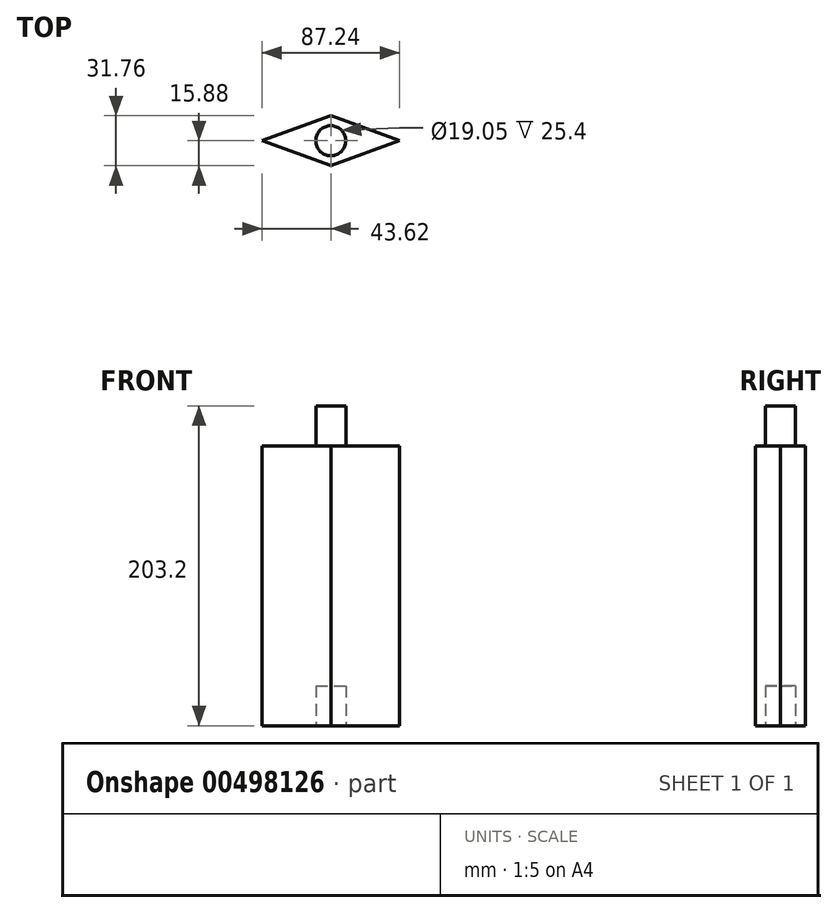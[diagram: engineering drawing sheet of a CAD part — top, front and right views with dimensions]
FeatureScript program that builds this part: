
annotation { "Feature Type Name" : "Feature", "Feature Type Description" : "" }
export const myFeature = defineFeature(function(context is Context, id is Id, definition is map)
    precondition{}
    {
        {
            var Q0;
            Q0=qCreatedBy(makeId("Top.planeOp"),FACE);
            var sketch = newSketch(context, id + "F0", { "sketchPlane" : qUnion([Q0])});
            skLineSegment(sketch, "E0.bottom", {"start": v(50.8, 15.88) * mm, "end": v(-50.8, 15.88) * mm});
            skLineSegment(sketch, "E0.top", {"start": v(50.8, -15.88) * mm, "end": v(-50.8, -15.88) * mm});
            skLineSegment(sketch, "E0.left", {"start": v(50.8, 15.88) * mm, "end": v(50.8, -15.88) * mm});
            skLineSegment(sketch, "E0.right", {"start": v(-50.8, 15.88) * mm, "end": v(-50.8, -15.88) * mm});
            skPoint(sketch, "E0.middle", {"position": v(0, 0) * mm});
            skSolve(sketch);
        }
        {
            var Q0;
            Q0=makeQuery(id+"F0.imprint","IMPRINT",FACE,{"disambiguationData":[TD([[makeQuery(id+"F0.imprint","IMPRINT",EDGE,{"derivedFrom":sQuery(id+"F0.wireOp",EDGE,"E0.bottom")}),1.0]])]});
            extrude(context, id + "F1", {"entities" : qUnion([Q0]), "depth" : 177.8 * mm, "offsetDistance" : 25.4 * mm});
        }
        {
            var Q0;
            Q0=makeQuery(id+"F1.opExtrude","SWEPT_EDGE",EDGE,{"disambiguationData":[OSD([sQuery(id+"F0.wireOp",EDGE,"E0.bottom"),sQuery(id+"F0.wireOp",EDGE,"E0.left")])]});
            var Q1;
            Q1=makeQuery(id+"F1.opExtrude","SWEPT_EDGE",EDGE,{"disambiguationData":[OSD([sQuery(id+"F0.wireOp",EDGE,"E0.top"),sQuery(id+"F0.wireOp",EDGE,"E0.left")])]});
            var Q2;
            Q2=makeQuery(id+"F1.opExtrude","SWEPT_EDGE",EDGE,{"disambiguationData":[OSD([sQuery(id+"F0.wireOp",EDGE,"E0.top"),sQuery(id+"F0.wireOp",EDGE,"E0.right")])]});
            var Q3;
            Q3=makeQuery(id+"F1.opExtrude","SWEPT_EDGE",EDGE,{"disambiguationData":[OSD([sQuery(id+"F0.wireOp",EDGE,"E0.bottom"),sQuery(id+"F0.wireOp",EDGE,"E0.right")])]});
            chamfer(context, id + "F2", {"entities" : qUnion([Q0, Q1, Q2, Q3]), "chamferType" : ChamferType.OFFSET_ANGLE, "width" : 50.8 * mm, "oppositeDirection" : false, "angle" : 20 * degree, "tangentPropagation" : true});
        }
        {
            var Q0;
            Q0=makeQuery(id+"F1.opExtrude","CAP_FACE",FACE,{"disambiguationData":[OSD([sQuery(id+"F0.wireOp",EDGE,"E0.bottom"),sQuery(id+"F0.wireOp",EDGE,"E0.top"),sQuery(id+"F0.wireOp",EDGE,"E0.left"),sQuery(id+"F0.wireOp",EDGE,"E0.right")])],"isStart":false});
            var sketch = newSketch(context, id + "F3", { "sketchPlane" : qUnion([Q0])});
            skCircle(sketch, "E1", {"center": v(0, 0) * mm, "radius": 9.53 * mm});
            skSolve(sketch);
        }
        {
            var Q0;
            Q0=qSketchRegion(id+"F3",true);
            extrude(context, id + "F4", {"entities" : qUnion([Q0]), "operationType" : NewBodyOperationType.ADD, "depth" : 25.4 * mm, "offsetDistance" : 25.4 * mm});
        }
        {
            var Q0;
            Q0=makeQuery(id+"F1.opExtrude","CAP_FACE",FACE,{"disambiguationData":[OSD([sQuery(id+"F0.wireOp",EDGE,"E0.bottom"),sQuery(id+"F0.wireOp",EDGE,"E0.top"),sQuery(id+"F0.wireOp",EDGE,"E0.left"),sQuery(id+"F0.wireOp",EDGE,"E0.right")])],"isStart":true});
            var sketch = newSketch(context, id + "F5", { "sketchPlane" : qUnion([Q0])});
            skCircle(sketch, "E2", {"center": v(0, 0) * mm, "radius": 9.53 * mm});
            skSolve(sketch);
        }
        {
            var Q0;
            Q0=qSketchRegion(id+"F5",true);
            extrude(context, id + "F6", {"entities" : qUnion([Q0]), "operationType" : NewBodyOperationType.REMOVE, "oppositeDirection" : true, "depth" : 25.4 * mm, "offsetDistance" : 25.4 * mm});
        }
    });
